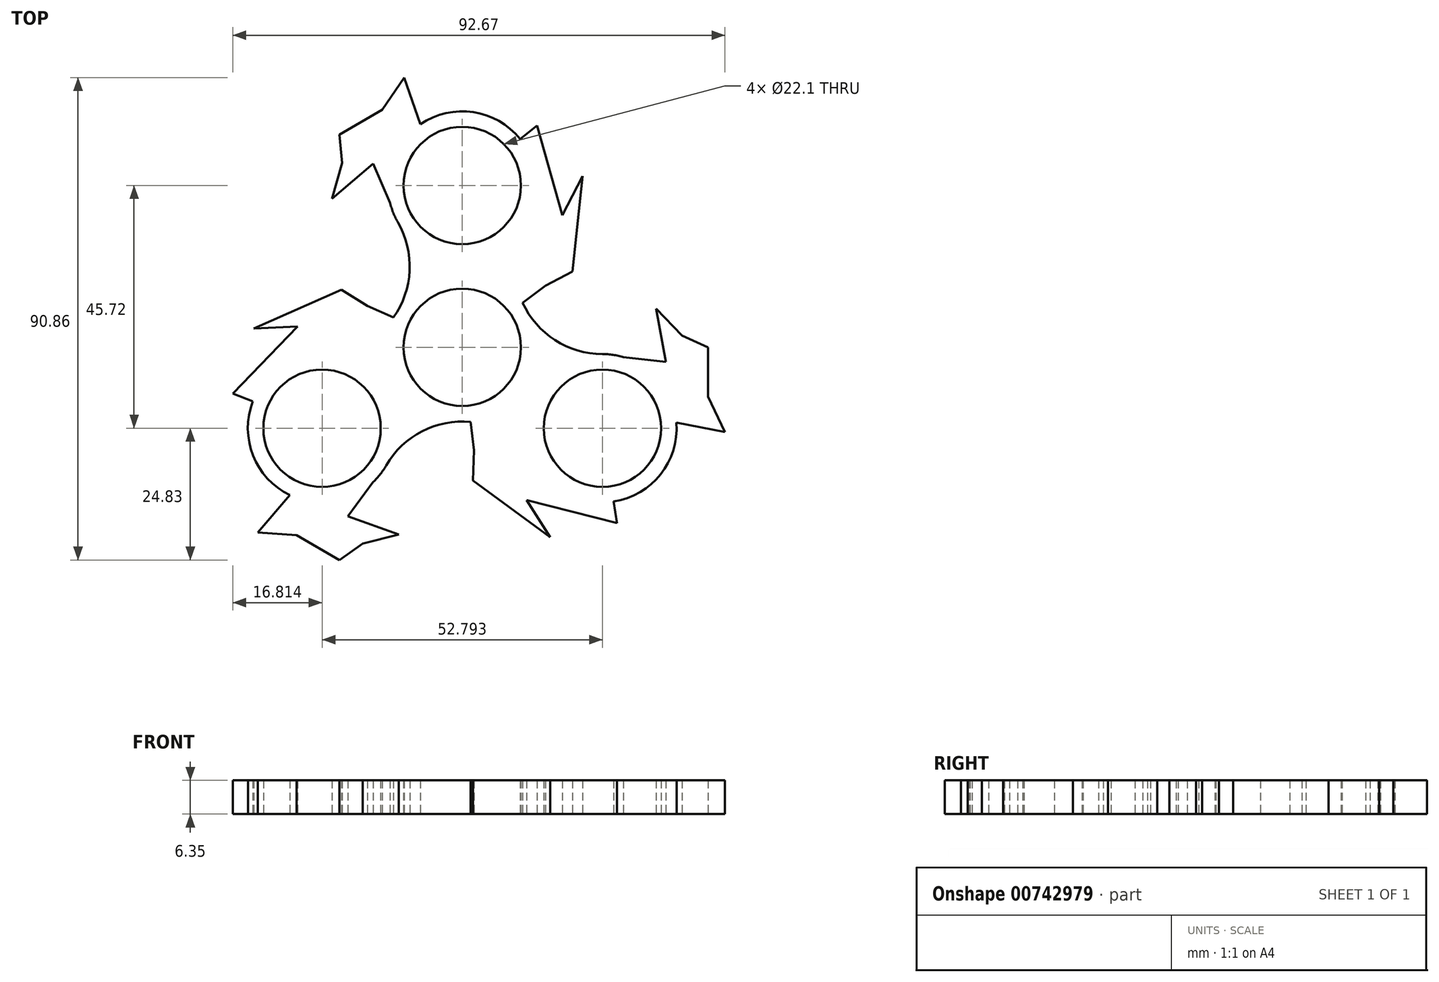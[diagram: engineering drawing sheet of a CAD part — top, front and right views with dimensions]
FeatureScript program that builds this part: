
annotation { "Feature Type Name" : "Feature", "Feature Type Description" : "" }
export const myFeature = defineFeature(function(context is Context, id is Id, definition is map)
    precondition{}
    {
        {
            var Q0;
            Q0=qCreatedBy(makeId("Top.planeOp"),FACE);
            var sketch = newSketch(context, id + "F0", { "sketchPlane" : qUnion([Q0])});
            skCircle(sketch, "E0", {"center": v(0, 0) * mm, "radius": 13.97 * mm});
            skCircle(sketch, "E1", {"center": v(0, 0) * mm, "radius": 11.05 * mm});
            skLineSegment(sketch, "E2", {"start": v(0, 0) * mm, "end": v(0, 30.48) * mm});
            skCircle(sketch, "E3", {"center": v(0, 30.48) * mm, "radius": 13.97 * mm});
            skCircle(sketch, "E4", {"center": v(0, 30.48) * mm, "radius": 11.05 * mm});
            skLineSegment(sketch, "E5.1.0", {"start": v(0, 0) * mm, "end": v(-26.4, -15.24) * mm});
            skCircle(sketch, "E5.1.1", {"center": v(-26.4, -15.24) * mm, "radius": 11.05 * mm});
            skLineSegment(sketch, "E5.2.0", {"start": v(0, 0) * mm, "end": v(26.4, -15.24) * mm});
            skCircle(sketch, "E5.2.1", {"center": v(26.4, -15.24) * mm, "radius": 11.05 * mm});
            skCircle(sketch, "E6.1.1", {"center": v(-26.4, -15.24) * mm, "radius": 13.97 * mm});
            skCircle(sketch, "E6.2.1", {"center": v(26.4, -15.24) * mm, "radius": 13.97 * mm});
            skLineSegment(sketch, "E7", {"start": v(0, 0) * mm, "end": v(0, -30.48) * mm});
            skArc(sketch, "E8", {"start": v(14.3, -22.23) * mm, "mid": v(0, -13.97) * mm, "end": v(-14.3, -22.22) * mm});
            skArc(sketch, "E9.1.1", {"start": v(12.1, 23.5) * mm, "mid": v(12.1, 6.98) * mm, "end": v(26.4, -1.27) * mm});
            skArc(sketch, "E9.2.1", {"start": v(-26.4, -1.27) * mm, "mid": v(-12.1, 6.99) * mm, "end": v(-12.1, 23.5) * mm});
            skPoint(sketch, "E10", {"position": v(-26.74, 31.75) * mm});
            skPoint(sketch, "E11", {"position": v(26.75, 31.75) * mm});
            skArc(sketch, "E12.1.1", {"start": v(14.3, -22.22) * mm, "mid": v(0, -13.97) * mm, "end": v(-14.3, -22.22) * mm});
            skArc(sketch, "E12.2.2", {"start": v(14.3, -22.22) * mm, "mid": v(0, -13.97) * mm, "end": v(-14.3, -22.22) * mm});
            skPoint(sketch, "E13.orphan", {"position": v(-40.87, 7.3) * mm});
            skPoint(sketch, "E14.orphan", {"position": v(40.86, 7.28) * mm});
            skPoint(sketch, "E15.orphan", {"position": v(14.12, -39.04) * mm});
            skPoint(sketch, "E16.orphan", {"position": v(-14.12, -39.03) * mm});
            skLineSegment(sketch, "E17", {"start": v(-33.44, 0) * mm, "end": v(-17.86, 7.79) * mm});
            skLineSegment(sketch, "E18", {"start": v(-17.86, 7.79) * mm, "end": v(-22.75, 10.84) * mm});
            skLineSegment(sketch, "E19", {"start": v(-22.75, 10.84) * mm, "end": v(-39.24, 3.51) * mm});
            skLineSegment(sketch, "E20", {"start": v(-39.24, 3.51) * mm, "end": v(-31, 3.9) * mm});
            skPoint(sketch, "E20.endSnap0", {"position": v(-25.65, 3.9) * mm});
            skPoint(sketch, "E20.endSnap1", {"position": v(-31, 7.18) * mm});
            skLineSegment(sketch, "E21", {"start": v(-31, 3.9) * mm, "end": v(-43.21, -8.7) * mm});
            skLineSegment(sketch, "E22", {"start": v(-43.21, -8.7) * mm, "end": v(-33.44, 0) * mm});
            skLineSegment(sketch, "E23", {"start": v(-17.86, 7.79) * mm, "end": v(-12.8, 5.58) * mm});
            skLineSegment(sketch, "E24", {"start": v(-43.21, -8.7) * mm, "end": v(-39.42, -10.18) * mm});
            skLineSegment(sketch, "E25.1.1", {"start": v(1.99, -25.12) * mm, "end": v(16.58, -35.74) * mm});
            skLineSegment(sketch, "E25.2.1", {"start": v(20.76, 14.28) * mm, "end": v(22.66, 32.23) * mm});
            skLineSegment(sketch, "E26.1.1", {"start": v(2.19, -19.37) * mm, "end": v(1.99, -25.12) * mm});
            skLineSegment(sketch, "E26.2.1", {"start": v(15.68, 11.58) * mm, "end": v(20.76, 14.28) * mm});
            skLineSegment(sketch, "E27.1.1", {"start": v(16.72, -28.96) * mm, "end": v(2.19, -19.37) * mm});
            skLineSegment(sketch, "E27.2.1", {"start": v(16.72, 28.96) * mm, "end": v(15.68, 11.58) * mm});
            skLineSegment(sketch, "E28.1.1", {"start": v(16.58, -35.74) * mm, "end": v(12.13, -28.8) * mm});
            skLineSegment(sketch, "E28.2.1", {"start": v(22.66, 32.23) * mm, "end": v(18.87, 24.9) * mm});
            skLineSegment(sketch, "E29.1.1", {"start": v(29.14, -33.07) * mm, "end": v(16.72, -28.96) * mm});
            skLineSegment(sketch, "E29.2.1", {"start": v(14.07, 41.77) * mm, "end": v(16.72, 28.96) * mm});
            skLineSegment(sketch, "E30.1.1", {"start": v(12.13, -28.8) * mm, "end": v(29.14, -33.07) * mm});
            skLineSegment(sketch, "E30.2.1", {"start": v(18.87, 24.9) * mm, "end": v(14.07, 41.77) * mm});
            skLineSegment(sketch, "E31.1.1", {"start": v(29.14, -33.07) * mm, "end": v(28.52, -29.05) * mm});
            skLineSegment(sketch, "E31.2.1", {"start": v(14.07, 41.77) * mm, "end": v(10.9, 39.23) * mm});
            skLineSegment(sketch, "E32.1.1", {"start": v(2.19, -19.37) * mm, "end": v(1.57, -13.88) * mm});
            skLineSegment(sketch, "E32.2.1", {"start": v(15.68, 11.58) * mm, "end": v(11.24, 8.3) * mm});
            skLineSegment(sketch, "E33", {"start": v(40.33, -14.2) * mm, "end": v(49.46, -15.92) * mm});
            skLineSegment(sketch, "E34", {"start": v(49.46, -15.92) * mm, "end": v(46.27, -9.31) * mm});
            skLineSegment(sketch, "E35", {"start": v(46.27, -9.31) * mm, "end": v(46.27, 0) * mm});
            skLineSegment(sketch, "E36", {"start": v(46.27, 0) * mm, "end": v(41.4, 2.24) * mm});
            skLineSegment(sketch, "E37", {"start": v(41.4, 2.24) * mm, "end": v(36.5, 7.28) * mm});
            skLineSegment(sketch, "E38", {"start": v(36.5, 7.28) * mm, "end": v(38.32, -2.76) * mm});
            skLineSegment(sketch, "E39", {"start": v(38.32, -2.76) * mm, "end": v(30.36, -1.84) * mm});
            skLineSegment(sketch, "E40.1.1", {"start": v(-16.77, 34.57) * mm, "end": v(-13.58, 27.22) * mm});
            skLineSegment(sketch, "E40.2.1", {"start": v(-21.55, -31.8) * mm, "end": v(-16.78, -25.37) * mm});
            skLineSegment(sketch, "E41.1.1", {"start": v(-24.56, 27.96) * mm, "end": v(-16.77, 34.57) * mm});
            skLineSegment(sketch, "E41.2.1", {"start": v(-11.94, -35.25) * mm, "end": v(-21.55, -31.8) * mm});
            skLineSegment(sketch, "E42.1.1", {"start": v(-22.64, 34.74) * mm, "end": v(-24.56, 27.96) * mm});
            skLineSegment(sketch, "E42.2.1", {"start": v(-18.77, -36.97) * mm, "end": v(-11.94, -35.25) * mm});
            skLineSegment(sketch, "E43.1.1", {"start": v(-23.13, 40.07) * mm, "end": v(-22.64, 34.74) * mm});
            skLineSegment(sketch, "E43.2.1", {"start": v(-23.13, -40.07) * mm, "end": v(-18.77, -36.97) * mm});
            skLineSegment(sketch, "E44.1.1", {"start": v(-15.07, 44.72) * mm, "end": v(-23.13, 40.07) * mm});
            skLineSegment(sketch, "E44.2.1", {"start": v(-31.2, -35.4) * mm, "end": v(-23.13, -40.07) * mm});
            skLineSegment(sketch, "E45.1.1", {"start": v(-7.87, 42.02) * mm, "end": v(-10.94, 50.8) * mm});
            skLineSegment(sketch, "E45.2.1", {"start": v(-32.45, -27.83) * mm, "end": v(-38.52, -34.87) * mm});
            skLineSegment(sketch, "E46.1.1", {"start": v(-10.94, 50.8) * mm, "end": v(-15.07, 44.72) * mm});
            skLineSegment(sketch, "E46.2.1", {"start": v(-38.52, -34.87) * mm, "end": v(-31.2, -35.4) * mm});
            skSolve(sketch);
        }
        {
            var Q0;
            Q0 = qSketchRegion(id + "F0", true);
            extrude(context, id + "F1", {"entities" : qUnion([Q0]), "depth" : 6.35 * mm, "offsetDistance" : 25.4 * mm});
        }
    });
